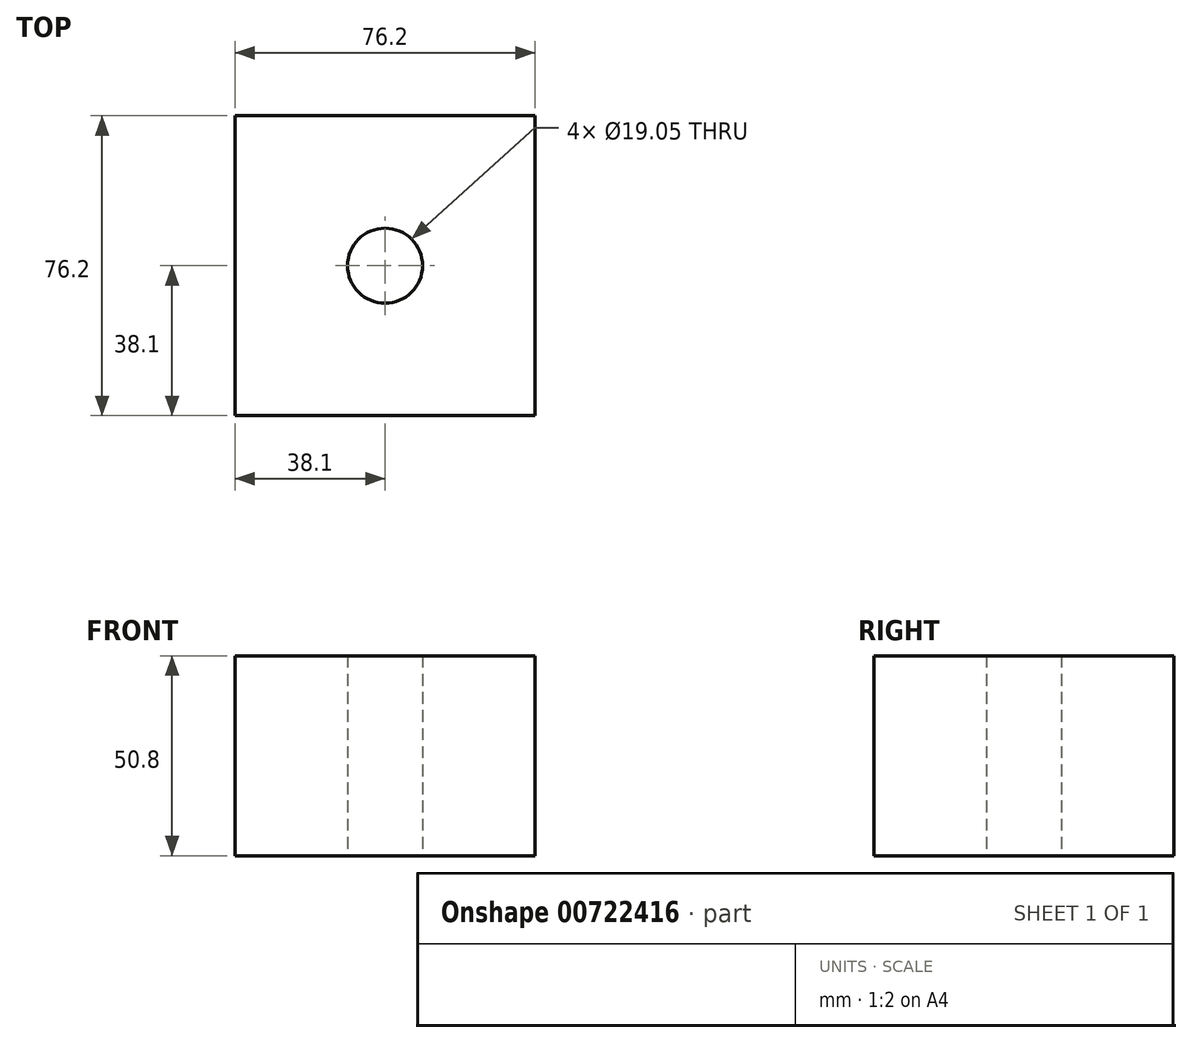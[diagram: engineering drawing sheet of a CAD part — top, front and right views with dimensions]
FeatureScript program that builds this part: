
annotation { "Feature Type Name" : "Feature", "Feature Type Description" : "" }
export const myFeature = defineFeature(function(context is Context, id is Id, definition is map)
    precondition{}
    {
        {
            var Q0;
            Q0=qCreatedBy(makeId("Top.planeOp"),FACE);
            var sketch = newSketch(context, id + "F0", { "sketchPlane" : qUnion([Q0])});
            skLineSegment(sketch, "E0.bottom", {"start": v(38.1, -38.1) * mm, "end": v(-38.1, -38.1) * mm});
            skLineSegment(sketch, "E0.top", {"start": v(38.1, 38.1) * mm, "end": v(-38.1, 38.1) * mm});
            skLineSegment(sketch, "E0.left", {"start": v(38.1, -38.1) * mm, "end": v(38.1, 38.1) * mm});
            skLineSegment(sketch, "E0.right", {"start": v(-38.1, -38.1) * mm, "end": v(-38.1, 38.1) * mm});
            skPoint(sketch, "E0.middle", {"position": v(0, 0) * mm});
            skCircle(sketch, "E1", {"center": v(0, 0) * mm, "radius": 9.53 * mm});
            skSolve(sketch);
        }
        {
            var Q0;
            Q0=makeQuery(id+"F0.imprint","IMPRINT",FACE,{"disambiguationData":[TD([[makeQuery(id+"F0.imprint","IMPRINT",EDGE,{"derivedFrom":sQuery(id+"F0.wireOp",EDGE,"E0.bottom")}),-1.0]])]});
            extrude(context, id + "F1", {"entities" : qUnion([Q0]), "depth" : 50.8 * mm, "offsetDistance" : 25.4 * mm});
        }
    });
